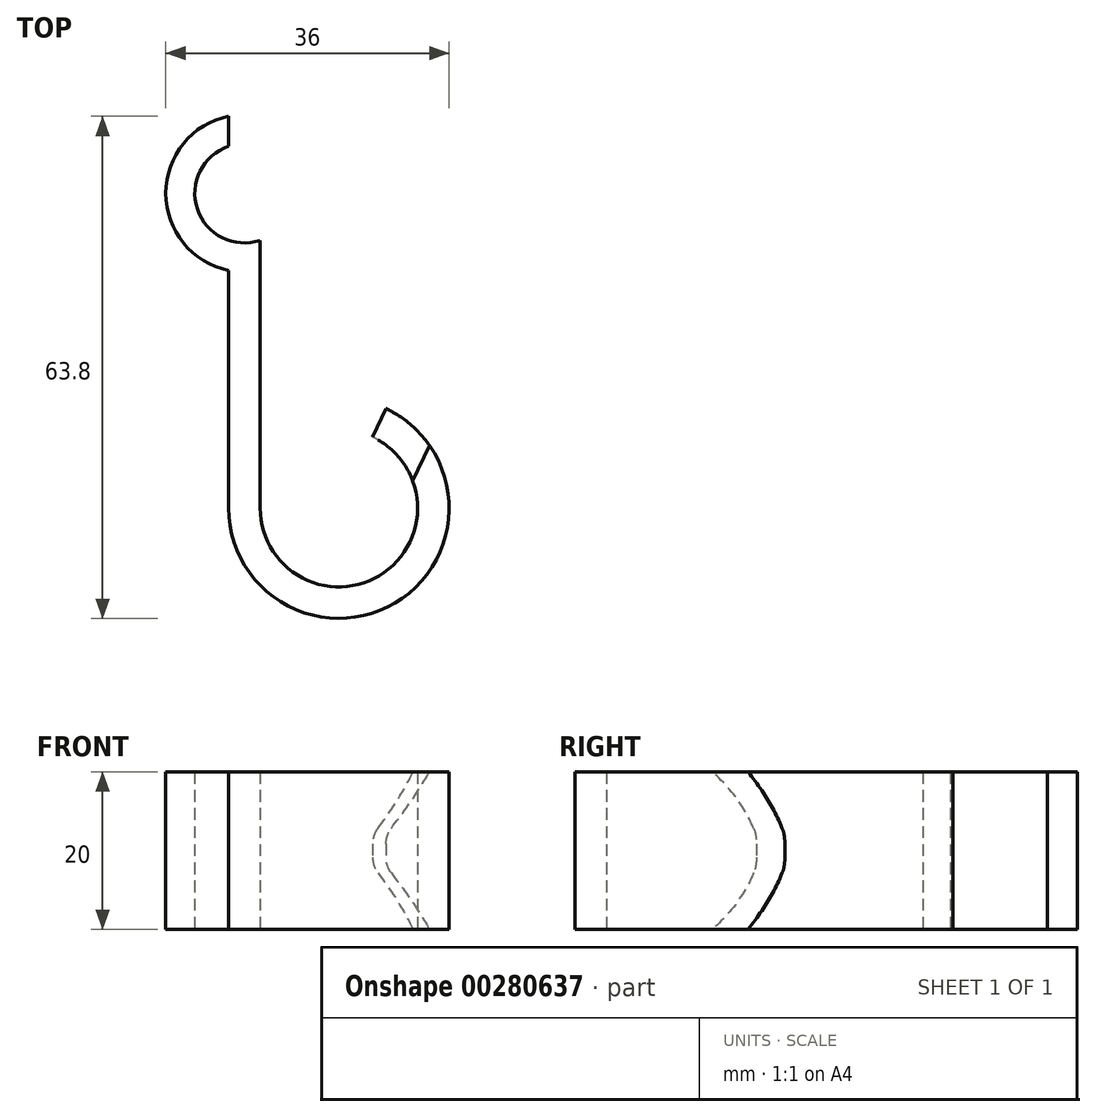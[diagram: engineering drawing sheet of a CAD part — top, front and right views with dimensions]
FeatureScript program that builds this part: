
annotation { "Feature Type Name" : "Feature", "Feature Type Description" : "" }
export const myFeature = defineFeature(function(context is Context, id is Id, definition is map)
    precondition{}
    {
        {
            var Q0;
            Q0=qCreatedBy(makeId("Top.planeOp"),FACE);
            var sketch = newSketch(context, id + "F0", { "sketchPlane" : qUnion([Q0])});
            skCircle(sketch, "E0", {"center": v(0, 0) * mm, "radius": 6.3 * mm});
            skCircle(sketch, "E1", {"center": v(0, 0) * mm, "radius": 10 * mm});
            skLineSegment(sketch, "E2.bottom", {"start": v(2, -40) * mm, "end": v(-2, -40) * mm});
            skLineSegment(sketch, "E2.top", {"start": v(2, 40) * mm, "end": v(-2, 40) * mm});
            skLineSegment(sketch, "E2.left", {"start": v(2, -40) * mm, "end": v(2, 40) * mm});
            skLineSegment(sketch, "E2.right", {"start": v(-2, -40) * mm, "end": v(-2, 40) * mm});
            skCircle(sketch, "E3", {"center": v(12, -40) * mm, "radius": 14 * mm});
            skCircle(sketch, "E4", {"center": v(12, -40) * mm, "radius": 10 * mm});
            skLineSegment(sketch, "E5", {"start": v(12, -40) * mm, "end": v(18, -27.35) * mm});
            skSolve(sketch);
        }
        {
            var Q0;
            {var subQ0=sQuery(id+"F0.wireOp",EDGE,"E2.left");var subQ1=sQuery(id+"F0.wireOp",EDGE,"E0");var subQ2=makeQuery(id+"F0.imprint","INTERSECT",VERTEX,{"disambiguationData":[OD(0.0)],"derivedFrom":[subQ1,subQ0]});Q0=makeQuery(id+"F0.imprint","IMPRINT",FACE,{"disambiguationData":[TD([[makeQuery(id+"F0.imprint","IMPRINT",EDGE,{"disambiguationData":[TD([[subQ2,1.0]])],"derivedFrom":subQ1}),-1.0]])]});}
            var Q1;
            {var subQ0=sQuery(id+"F0.wireOp",EDGE,"E2.right");var subQ1=sQuery(id+"F0.wireOp",EDGE,"E0");var subQ2=makeQuery(id+"F0.imprint","INTERSECT",VERTEX,{"disambiguationData":[OD(0.0)],"derivedFrom":[subQ1,subQ0]});Q1=makeQuery(id+"F0.imprint","IMPRINT",FACE,{"disambiguationData":[TD([[makeQuery(id+"F0.imprint","IMPRINT",EDGE,{"disambiguationData":[TD([[subQ2,1.0]])],"derivedFrom":subQ1}),-1.0]])]});}
            var Q2;
            {var subQ0=sQuery(id+"F0.wireOp",EDGE,"E2.right");var subQ1=sQuery(id+"F0.wireOp",EDGE,"E0");var subQ2=makeQuery(id+"F0.imprint","INTERSECT",VERTEX,{"disambiguationData":[OD(0.0)],"derivedFrom":[subQ1,subQ0]});Q2=makeQuery(id+"F0.imprint","IMPRINT",FACE,{"disambiguationData":[TD([[makeQuery(id+"F0.imprint","IMPRINT",EDGE,{"disambiguationData":[TD([[subQ2,-1.0]])],"derivedFrom":subQ1}),-1.0]])]});}
            var Q3;
            {var subQ0=sQuery(id+"F0.wireOp",EDGE,"E2.right");var subQ1=sQuery(id+"F0.wireOp",EDGE,"E0");var subQ2=makeQuery(id+"F0.imprint","INTERSECT",VERTEX,{"disambiguationData":[OD(1.0)],"derivedFrom":[subQ1,subQ0]});Q3=makeQuery(id+"F0.imprint","IMPRINT",FACE,{"disambiguationData":[TD([[makeQuery(id+"F0.imprint","IMPRINT",EDGE,{"disambiguationData":[TD([[subQ2,-1.0]])],"derivedFrom":subQ1}),-1.0]])]});}
            var Q4;
            {var subQ0=sQuery(id+"F0.wireOp",EDGE,"E2.right");var subQ1=sQuery(id+"F0.wireOp",EDGE,"E1");var subQ2=makeQuery(id+"F0.imprint","INTERSECT",VERTEX,{"disambiguationData":[OD(1.0)],"derivedFrom":[subQ1,subQ0]});Q4=makeQuery(id+"F0.imprint","IMPRINT",FACE,{"disambiguationData":[TD([[makeQuery(id+"F0.imprint","IMPRINT",EDGE,{"disambiguationData":[TD([[subQ2,-1.0]])],"derivedFrom":subQ1}),-1.0]])]});}
            var Q5;
            {var subQ0=sQuery(id+"F0.wireOp",EDGE,"E2.bottom");Q5=makeQuery(id+"F0.imprint","IMPRINT",FACE,{"disambiguationData":[TD([[makeQuery(id+"F0.imprint","IMPRINT",EDGE,{"derivedFrom":subQ0}),-1.0]])]});}
            var Q6;
            {var subQ0=sQuery(id+"F0.wireOp",EDGE,"E2.bottom");Q6=makeQuery(id+"F0.imprint","IMPRINT",FACE,{"disambiguationData":[TD([[makeQuery(id+"F0.imprint","IMPRINT",EDGE,{"derivedFrom":subQ0}),1.0]])]});}
            extrude(context, id + "F1", {"entities" : qUnion([Q0, Q1, Q2, Q3, Q4, Q5, Q6]), "depth" : 20 * mm});
        }
        {
            var Q0;
            Q0=makeQuery(id+"F1.opExtrude","CAP_EDGE",EDGE,{"disambiguationData":[OSD([sQuery(id+"F0.wireOp",EDGE,"E5")])],"isStart":false});
            var Q1;
            Q1=makeQuery(id+"F1.opExtrude","CAP_EDGE",EDGE,{"disambiguationData":[OSD([sQuery(id+"F0.wireOp",EDGE,"E5")])],"isStart":true});
            chamfer(context, id + "F2", {"entities" : qUnion([Q0, Q1]), "chamferType" : ChamferType.TWO_OFFSETS, "width1" : 8 * mm, "oppositeDirection" : false, "width2" : 7 * mm, "tangentPropagation" : true});
        }
        {
            var Q0;
            {var subQ0=sQuery(id+"F0.wireOp",EDGE,"E5");Q0=makeQuery(id+"F2.opChamfer","BLEND_EDGE",EDGE,{"blendedFrom":[makeQuery(id+"F1.opExtrude","CAP_EDGE",EDGE,{"disambiguationData":[OSD([subQ0])],"isStart":false}),makeQuery(id+"F1.opExtrude","SWEPT_FACE",FACE,{"disambiguationData":[OSD([subQ0])]})],"blendedInto":[makeQuery(id+"F1.opExtrude","SWEPT_FACE",FACE,{"disambiguationData":[OSD([subQ0])]})]});}
            var Q1;
            {var subQ0=sQuery(id+"F0.wireOp",EDGE,"E5");Q1=makeQuery(id+"F2.opChamfer","BLEND_EDGE",EDGE,{"blendedFrom":[makeQuery(id+"F1.opExtrude","CAP_EDGE",EDGE,{"disambiguationData":[OSD([subQ0])],"isStart":true}),makeQuery(id+"F1.opExtrude","SWEPT_FACE",FACE,{"disambiguationData":[OSD([subQ0])]})],"blendedInto":[makeQuery(id+"F1.opExtrude","SWEPT_FACE",FACE,{"disambiguationData":[OSD([subQ0])]})]});}
            fillet(context, id + "F3", {"entities" : qUnion([Q0, Q1]), "radius" : 3 * mm, "tangentPropagation" : true, "allowEdgeOverflow" : false});
        }
    });
